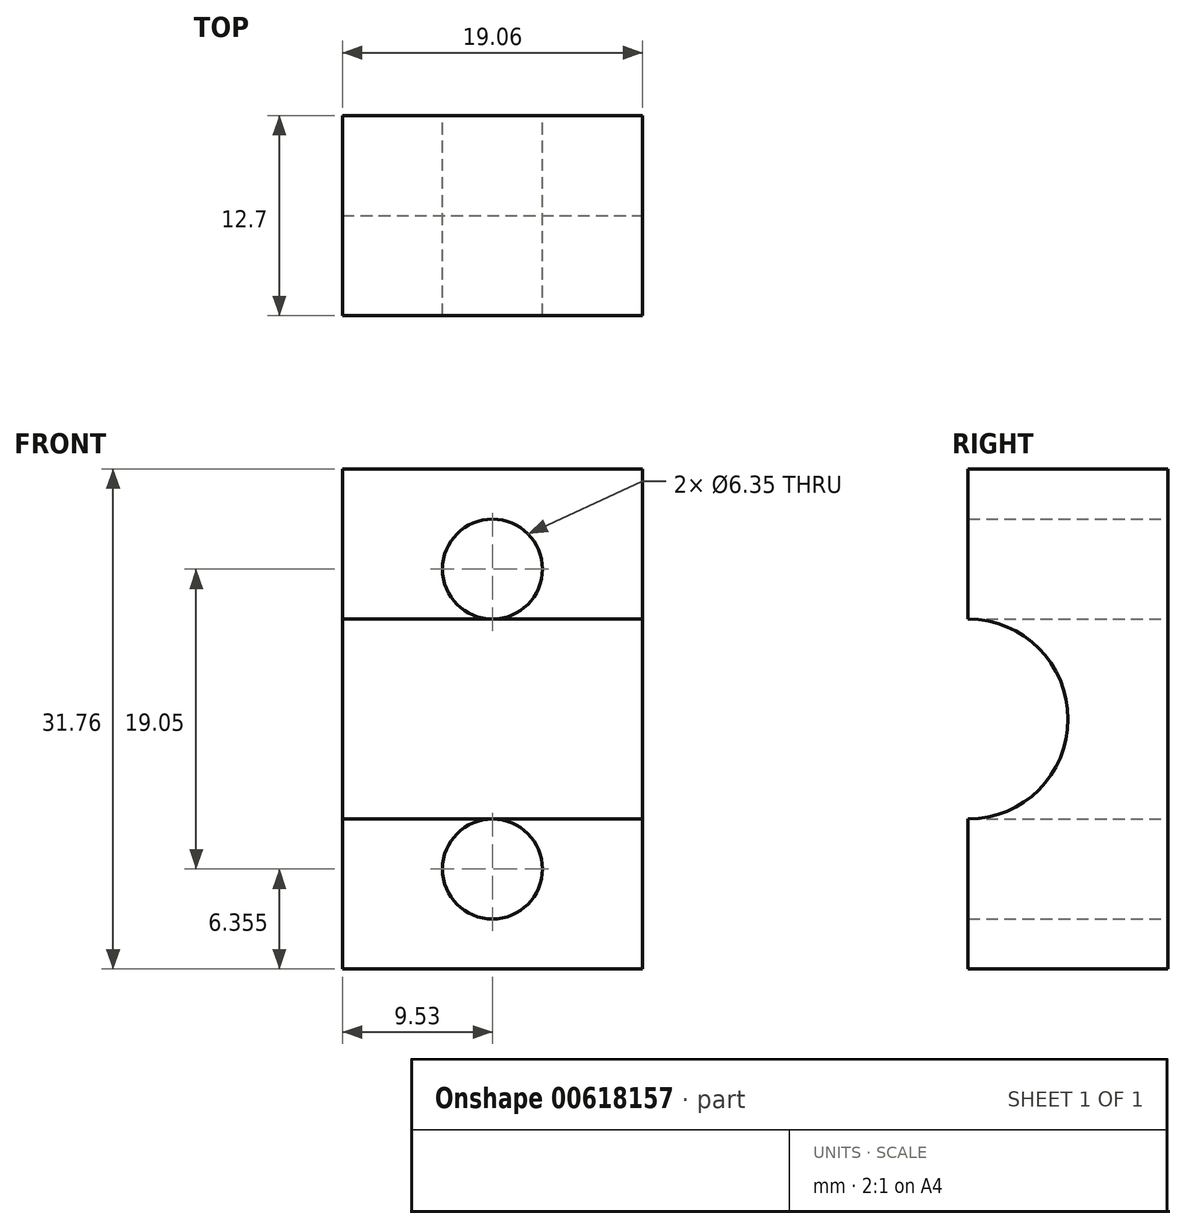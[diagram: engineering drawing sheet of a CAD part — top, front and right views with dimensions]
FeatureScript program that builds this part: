
annotation { "Feature Type Name" : "Feature", "Feature Type Description" : "" }
export const myFeature = defineFeature(function(context is Context, id is Id, definition is map)
    precondition{}
    {
        {
            var Q0;
            Q0=qCreatedBy(makeId("Front.planeOp"),FACE);
            var sketch = newSketch(context, id + "F0", { "sketchPlane" : qUnion([Q0])});
            skLineSegment(sketch, "E0.bottom", {"start": v(9.53, 15.88) * mm, "end": v(-9.53, 15.88) * mm});
            skLineSegment(sketch, "E0.top", {"start": v(9.53, -15.88) * mm, "end": v(-9.53, -15.88) * mm});
            skLineSegment(sketch, "E0.left", {"start": v(9.53, 15.88) * mm, "end": v(9.53, -15.88) * mm});
            skLineSegment(sketch, "E0.right", {"start": v(-9.53, 15.88) * mm, "end": v(-9.53, -15.88) * mm});
            skPoint(sketch, "E0.middle", {"position": v(0, 0) * mm});
            skLineSegment(sketch, "E1", {"start": v(0, 15.88) * mm, "end": v(0, -15.88) * mm, "construction": true});
            skCircle(sketch, "E2", {"center": v(0, 9.52) * mm, "radius": 3.18 * mm});
            skCircle(sketch, "E3", {"center": v(0, -9.52) * mm, "radius": 3.18 * mm});
            skSolve(sketch);
        }
        {
            var Q0;
            Q0=qSketchRegion(id+"F0",true);
            extrude(context, id + "F1", {"entities" : qUnion([Q0]), "depth" : 12.7 * mm});
        }
        {
            var Q0;
            Q0=makeQuery(id+"F1.opExtrude","SWEPT_FACE",FACE,{"disambiguationData":[OSD([sQuery(id+"F0.wireOp",EDGE,"E0.left")])]});
            var sketch = newSketch(context, id + "F2", { "sketchPlane" : qUnion([Q0])});
            skCircle(sketch, "E4", {"center": v(-12.7, 0) * mm, "radius": 6.35 * mm});
            skSolve(sketch);
        }
        {
            var Q0;
            Q0=qSketchRegion(id+"F2",true);
            extrude(context, id + "F3", {"entities" : qUnion([Q0]), "operationType" : NewBodyOperationType.REMOVE, "endBound" : BoundingType.THROUGH_ALL, "oppositeDirection" : true, "depth" : 25.4 * mm});
        }
    });
